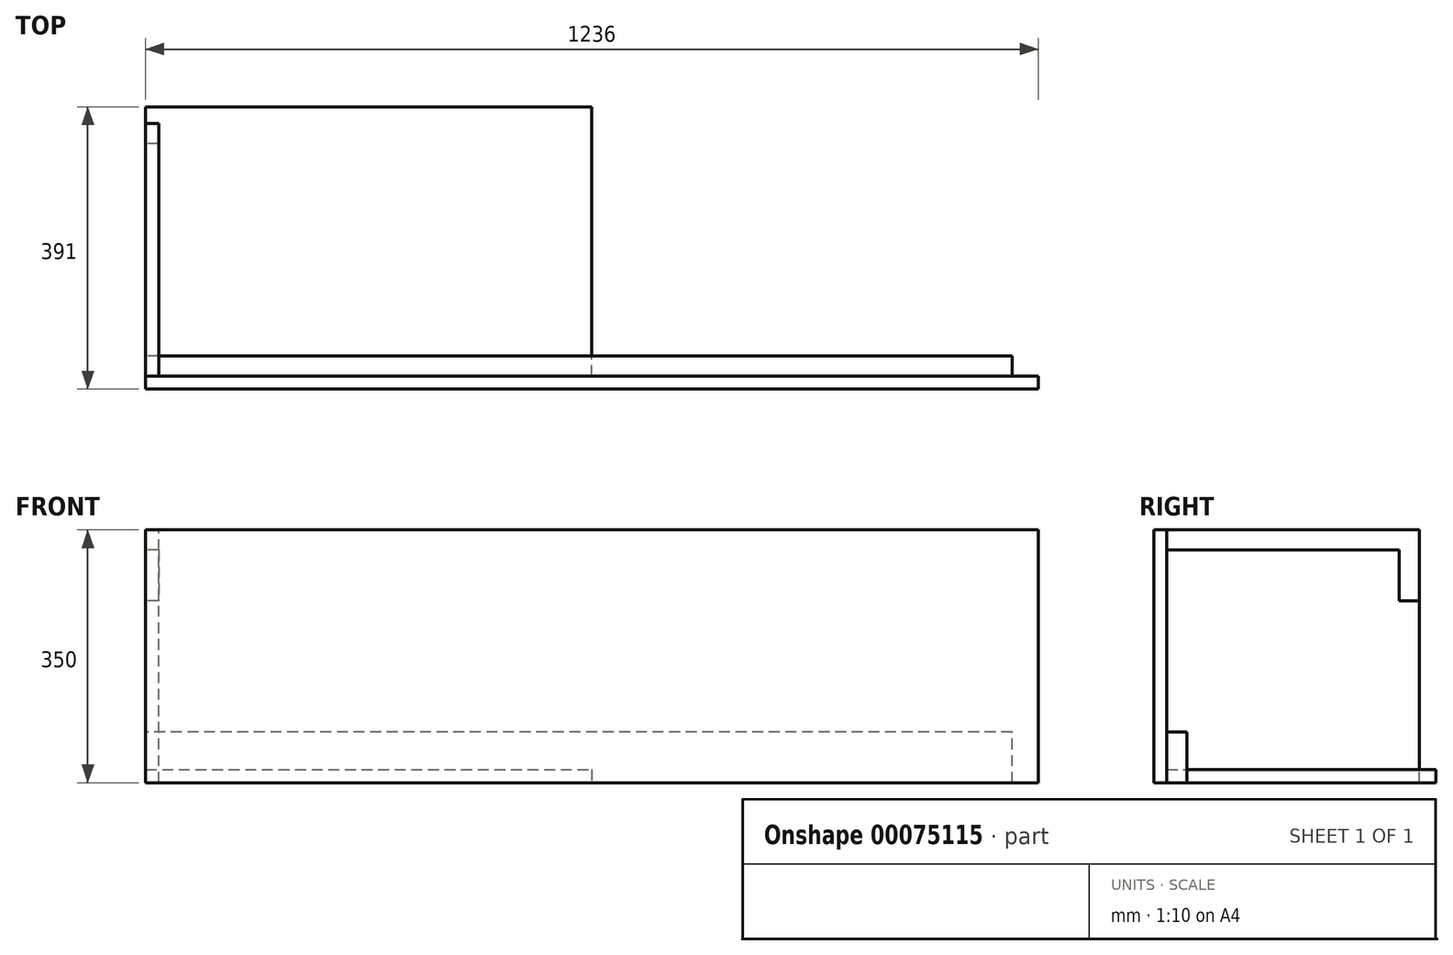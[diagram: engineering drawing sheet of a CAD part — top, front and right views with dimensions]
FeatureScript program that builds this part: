
annotation { "Feature Type Name" : "Feature", "Feature Type Description" : "" }
export const myFeature = defineFeature(function(context is Context, id is Id, definition is map)
    precondition{}
    {
        {
            assignVariable(context, id + "F0", {"name" : "length", "anyValue" : 1200});
        }
        {
            var Q0;
            Q0=qCreatedBy(makeId("Right.planeOp"),FACE);
            var sketch = newSketch(context, id + "F1", { "sketchPlane" : qUnion([Q0])});
            skLineSegment(sketch, "E0.bottom", {"start": v(0, 0) * mm, "end": v(350, 0) * mm});
            skLineSegment(sketch, "E0.top", {"start": v(0, 350) * mm, "end": v(350, 350) * mm});
            skLineSegment(sketch, "E0.left", {"start": v(0, 0) * mm, "end": v(0, 350) * mm});
            skLineSegment(sketch, "E0.right", {"start": v(350, 0) * mm, "end": v(350, 350) * mm});
            skSolve(sketch);
        }
        {
            var Q0;
            Q0=makeQuery(id+"F1.imprint","IMPRINT",FACE,{"disambiguationData":[TD([[makeQuery(id+"F1.imprint","IMPRINT",EDGE,{"derivedFrom":sQuery(id+"F1.wireOp",EDGE,"E0.bottom")}),1.0]])]});
            extrude(context, id + "F2", {"entities" : qUnion([Q0]), "depth" : 18 * mm});
        }
        {
            var Q0;
            Q0=qCreatedBy(makeId("Right.planeOp"),FACE);
            var sketch = newSketch(context, id + "F3", { "sketchPlane" : qUnion([Q0])});
            skLineSegment(sketch, "E1.bottom", {"start": v(0, 0) * mm, "end": v(28, 0) * mm});
            skLineSegment(sketch, "E1.top", {"start": v(0, 70) * mm, "end": v(28, 70) * mm});
            skLineSegment(sketch, "E1.left", {"start": v(0, 0) * mm, "end": v(0, 70) * mm});
            skLineSegment(sketch, "E1.right", {"start": v(28, 0) * mm, "end": v(28, 70) * mm});
            skSolve(sketch);
        }
        {
            var Q0;
            Q0 = qSketchRegion(id + "F3", true);
            extrude(context, id + "F4", {"entities" : qUnion([Q0]), "depth" : (getVariable(context, 'length')) * mm});
        }
        {
            var Q0;
            Q0=qCreatedBy(makeId("Right.planeOp"),FACE);
            var sketch = newSketch(context, id + "F5", { "sketchPlane" : qUnion([Q0])});
            skLineSegment(sketch, "E2.bottom", {"start": v(0, 0) * mm, "end": v(350, 0) * mm});
            skLineSegment(sketch, "E2.top", {"start": v(0, 322) * mm, "end": v(350, 322) * mm});
            skLineSegment(sketch, "E2.left", {"start": v(0, 0) * mm, "end": v(0, 322) * mm});
            skLineSegment(sketch, "E2.right", {"start": v(350, 0) * mm, "end": v(350, 322) * mm});
            skLineSegment(sketch, "E3.bottom", {"start": v(350, 322) * mm, "end": v(322, 322) * mm});
            skLineSegment(sketch, "E3.top", {"start": v(350, 252) * mm, "end": v(322, 252) * mm});
            skLineSegment(sketch, "E3.left", {"start": v(350, 322) * mm, "end": v(350, 252) * mm});
            skLineSegment(sketch, "E3.right", {"start": v(322, 322) * mm, "end": v(322, 252) * mm});
            skSolve(sketch);
        }
        {
            var Q0;
            Q0=makeQuery(id+"F5.imprint","IMPRINT",FACE,{"disambiguationData":[TD([[makeQuery(id+"F5.imprint","IMPRINT",EDGE,{"derivedFrom":sQuery(id+"F5.wireOp",EDGE,"E2.bottom")}),1.0]])]});
            extrude(context, id + "F6", {"entities" : qUnion([Q0]), "depth" : 18 * mm});
        }
        {
            var Q0;
            Q0=qCreatedBy(makeId("Front.planeOp"),FACE);
            var sketch = newSketch(context, id + "F7", { "sketchPlane" : qUnion([Q0])});
            skLineSegment(sketch, "E4.bottom", {"start": v(0, 0) * mm, "end": v(1236, 0) * mm});
            skLineSegment(sketch, "E4.top", {"start": v(0, 350) * mm, "end": v(1236, 350) * mm});
            skLineSegment(sketch, "E4.left", {"start": v(0, 0) * mm, "end": v(0, 350) * mm});
            skLineSegment(sketch, "E4.right", {"start": v(1236, 0) * mm, "end": v(1236, 350) * mm});
            skSolve(sketch);
        }
        {
            var Q0;
            Q0 = qSketchRegion(id + "F7", true);
            extrude(context, id + "F8", {"entities" : qUnion([Q0]), "depth" : 18 * mm});
        }
        {
            var Q0;
            Q0=qCreatedBy(makeId("Top.planeOp"),FACE);
            var sketch = newSketch(context, id + "F9", { "sketchPlane" : qUnion([Q0])});
            skLineSegment(sketch, "E5.bottom", {"start": v(0, 0) * mm, "end": v(618, 0) * mm});
            skLineSegment(sketch, "E5.top", {"start": v(0, 373) * mm, "end": v(618, 373) * mm});
            skLineSegment(sketch, "E5.left", {"start": v(0, 0) * mm, "end": v(0, 373) * mm});
            skLineSegment(sketch, "E5.right", {"start": v(618, 0) * mm, "end": v(618, 373) * mm});
            skSolve(sketch);
        }
        {
            var Q0;
            Q0 = qSketchRegion(id + "F9", true);
            extrude(context, id + "F10", {"entities" : qUnion([Q0]), "depth" : 18 * mm});
        }
    });
